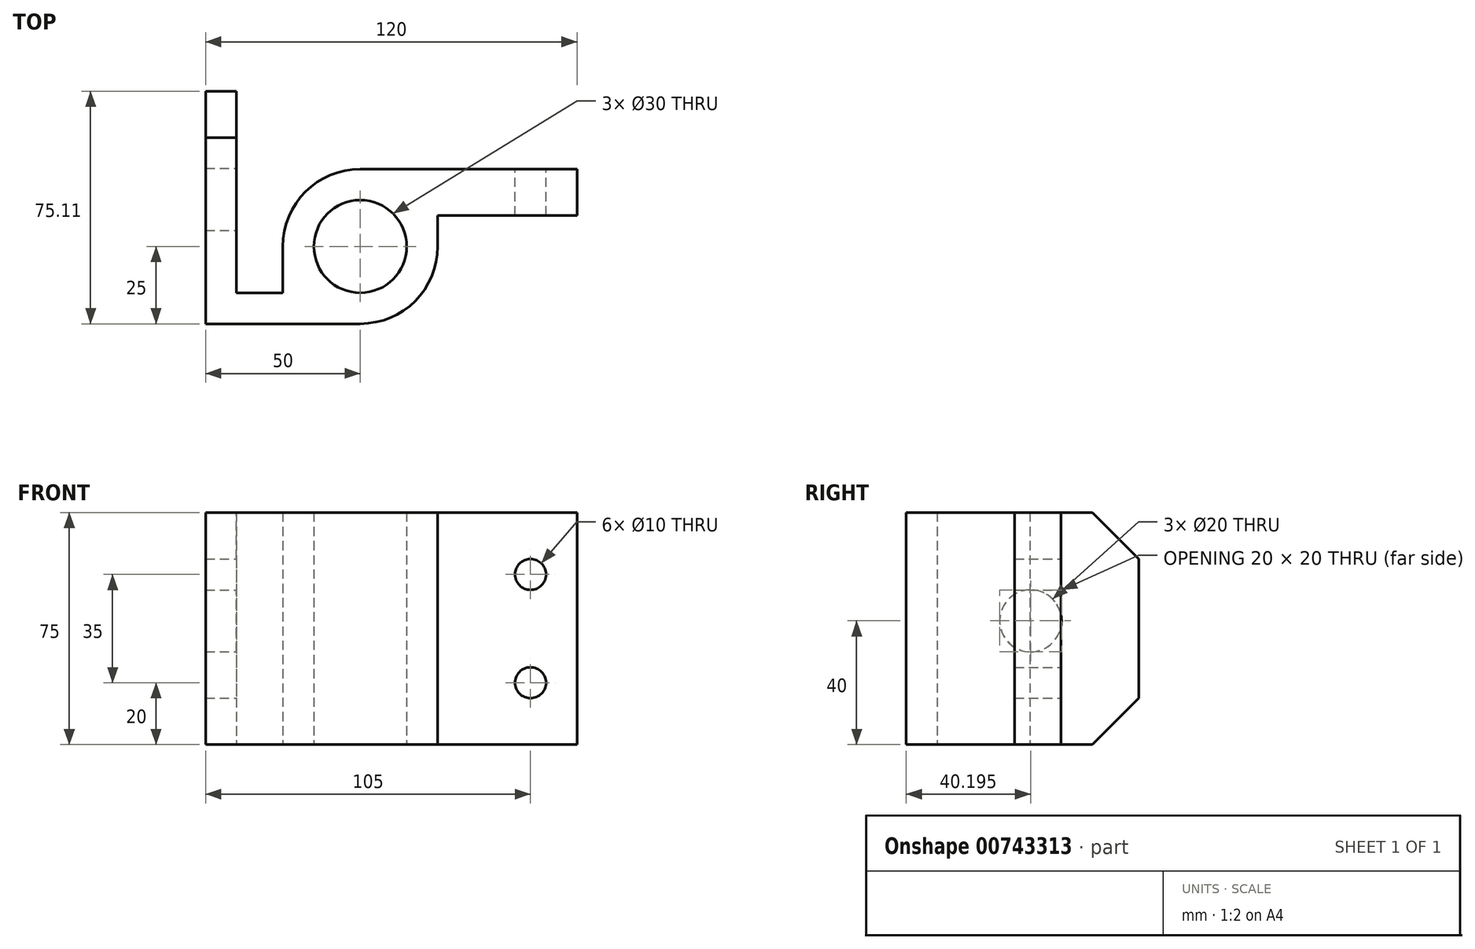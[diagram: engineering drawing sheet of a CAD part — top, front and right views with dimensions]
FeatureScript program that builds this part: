
annotation { "Feature Type Name" : "Feature", "Feature Type Description" : "" }
export const myFeature = defineFeature(function(context is Context, id is Id, definition is map)
    precondition{}
    {
        {
            var Q0;
            Q0=qCreatedBy(makeId("Top.planeOp"),FACE);
            var sketch = newSketch(context, id + "F0", { "sketchPlane" : qUnion([Q0])});
            skCircle(sketch, "E0", {"center": v(0, 0) * mm, "radius": 15 * mm});
            skArc(sketch, "E1", {"start": v(0, -25) * mm, "mid": v(17.68, -17.68) * mm, "end": v(25, 0) * mm});
            skLineSegment(sketch, "E2", {"start": v(0, -25) * mm, "end": v(-50, -25) * mm});
            skLineSegment(sketch, "E3", {"start": v(-50, -25) * mm, "end": v(-50, 50.1) * mm});
            skLineSegment(sketch, "E4", {"start": v(-50, 50.1) * mm, "end": v(-40, 50.1) * mm});
            skLineSegment(sketch, "E5", {"start": v(-40, 50.1) * mm, "end": v(-40, -15) * mm});
            skLineSegment(sketch, "E6", {"start": v(-25, -15) * mm, "end": v(-40, -15) * mm});
            skLineSegment(sketch, "E7", {"start": v(-25, 0) * mm, "end": v(-25, -15) * mm});
            skLineSegment(sketch, "E8", {"start": v(0, 25) * mm, "end": v(70, 25) * mm});
            skLineSegment(sketch, "E9", {"start": v(70, 25) * mm, "end": v(70, 10) * mm});
            skLineSegment(sketch, "E10", {"start": v(70, 10) * mm, "end": v(25, 10) * mm});
            skLineSegment(sketch, "E11", {"start": v(25, 0) * mm, "end": v(25, 10) * mm});
            skPoint(sketch, "E12.orphan", {"position": v(0, -15) * mm});
            skArc(sketch, "E13.trimOffspring", {"start": v(0, 25) * mm, "mid": v(-17.68, 17.68) * mm, "end": v(-25, 0) * mm});
            skSolve(sketch);
        }
        {
            var Q0;
            Q0=makeQuery(id+"F0.imprint","IMPRINT",FACE,{"disambiguationData":[TD([[makeQuery(id+"F0.imprint","IMPRINT",EDGE,{"derivedFrom":sQuery(id+"F0.wireOp",EDGE,"E0")}),-1.0]])]});
            extrude(context, id + "F1", {"entities" : qUnion([Q0]), "depth" : 75 * mm, "offsetDistance" : 25 * mm});
        }
        {
            var Q0;
            Q0=makeQuery(id+"F1.opExtrude","SWEPT_FACE",FACE,{"disambiguationData":[OSD([sQuery(id+"F0.wireOp",EDGE,"E8")])]});
            var sketch = newSketch(context, id + "F2", { "sketchPlane" : qUnion([Q0])});
            skPoint(sketch, "E14", {"position": v(-70, 0) * mm});
            skPoint(sketch, "E15", {"position": v(-55, 0) * mm});
            skPoint(sketch, "E16", {"position": v(-55, 20) * mm});
            skPoint(sketch, "E17", {"position": v(-55, 55) * mm});
            skCircle(sketch, "E18", {"center": v(-55, 20) * mm, "radius": 5 * mm});
            skCircle(sketch, "E19", {"center": v(-55, 55) * mm, "radius": 5 * mm});
            skSolve(sketch);
        }
        {
            var Q0;
            Q0=makeQuery(id+"F2.imprint","IMPRINT",FACE,{"disambiguationData":[TD([[makeQuery(id+"F2.imprint","IMPRINT",EDGE,{"derivedFrom":sQuery(id+"F2.wireOp",EDGE,"E18")}),1.0]])]});
            var Q1;
            Q1=makeQuery(id+"F2.imprint","IMPRINT",FACE,{"disambiguationData":[TD([[makeQuery(id+"F2.imprint","IMPRINT",EDGE,{"derivedFrom":sQuery(id+"F2.wireOp",EDGE,"E19")}),1.0]])]});
            extrude(context, id + "F3", {"entities" : qUnion([Q0, Q1]), "operationType" : NewBodyOperationType.REMOVE, "oppositeDirection" : true, "depth" : 15 * mm, "offsetDistance" : 25 * mm});
        }
        {
            var Q0;
            Q0=makeQuery(id+"F1.opExtrude","SWEPT_FACE",FACE,{"disambiguationData":[OSD([sQuery(id+"F0.wireOp",EDGE,"E5")])]});
            var sketch = newSketch(context, id + "F4", { "sketchPlane" : qUnion([Q0])});
            skPoint(sketch, "E20", {"position": v(15.2, 75) * mm});
            skPoint(sketch, "E21", {"position": v(15.2, 40) * mm});
            skPoint(sketch, "E22", {"position": v(50.1, 37.5) * mm});
            skCircle(sketch, "E23", {"center": v(15.2, 40) * mm, "radius": 10 * mm});
            skPoint(sketch, "E24", {"position": v(50.1, 75) * mm});
            skPoint(sketch, "E25", {"position": v(50.1, 60) * mm});
            skPoint(sketch, "E26", {"position": v(35.1, 75) * mm});
            skPoint(sketch, "E27", {"position": v(50.1, 0) * mm});
            skPoint(sketch, "E28", {"position": v(50.1, 15) * mm});
            skPoint(sketch, "E29", {"position": v(35.1, 0) * mm});
            skLineSegment(sketch, "E30", {"start": v(50.1, 60) * mm, "end": v(35.1, 75) * mm});
            skLineSegment(sketch, "E31", {"start": v(50.1, 15) * mm, "end": v(35.1, 0) * mm});
            skSolve(sketch);
        }
        {
            var Q0;
            Q0=makeQuery(id+"F4.imprint","IMPRINT",FACE,{"disambiguationData":[TD([[makeQuery(id+"F4.imprint","IMPRINT",EDGE,{"derivedFrom":sQuery(id+"F4.wireOp",EDGE,"E23")}),1.0]])]});
            var Q1;
            {var subQ0=sQuery(id+"F4.wireOp",EDGE,"E30");Q1=makeQuery(id+"F4.imprint","IMPRINT",FACE,{"disambiguationData":[TD([[makeQuery(id+"F4.imprint","IMPRINT",EDGE,{"derivedFrom":subQ0}),-1.0]])]});}
            var Q2;
            {var subQ0=sQuery(id+"F4.wireOp",EDGE,"E31");Q2=makeQuery(id+"F4.imprint","IMPRINT",FACE,{"disambiguationData":[TD([[makeQuery(id+"F4.imprint","IMPRINT",EDGE,{"derivedFrom":subQ0}),1.0]])]});}
            extrude(context, id + "F5", {"entities" : qUnion([Q0, Q1, Q2]), "operationType" : NewBodyOperationType.REMOVE, "oppositeDirection" : true, "depth" : 25 * mm, "offsetDistance" : 25 * mm});
        }
    });
